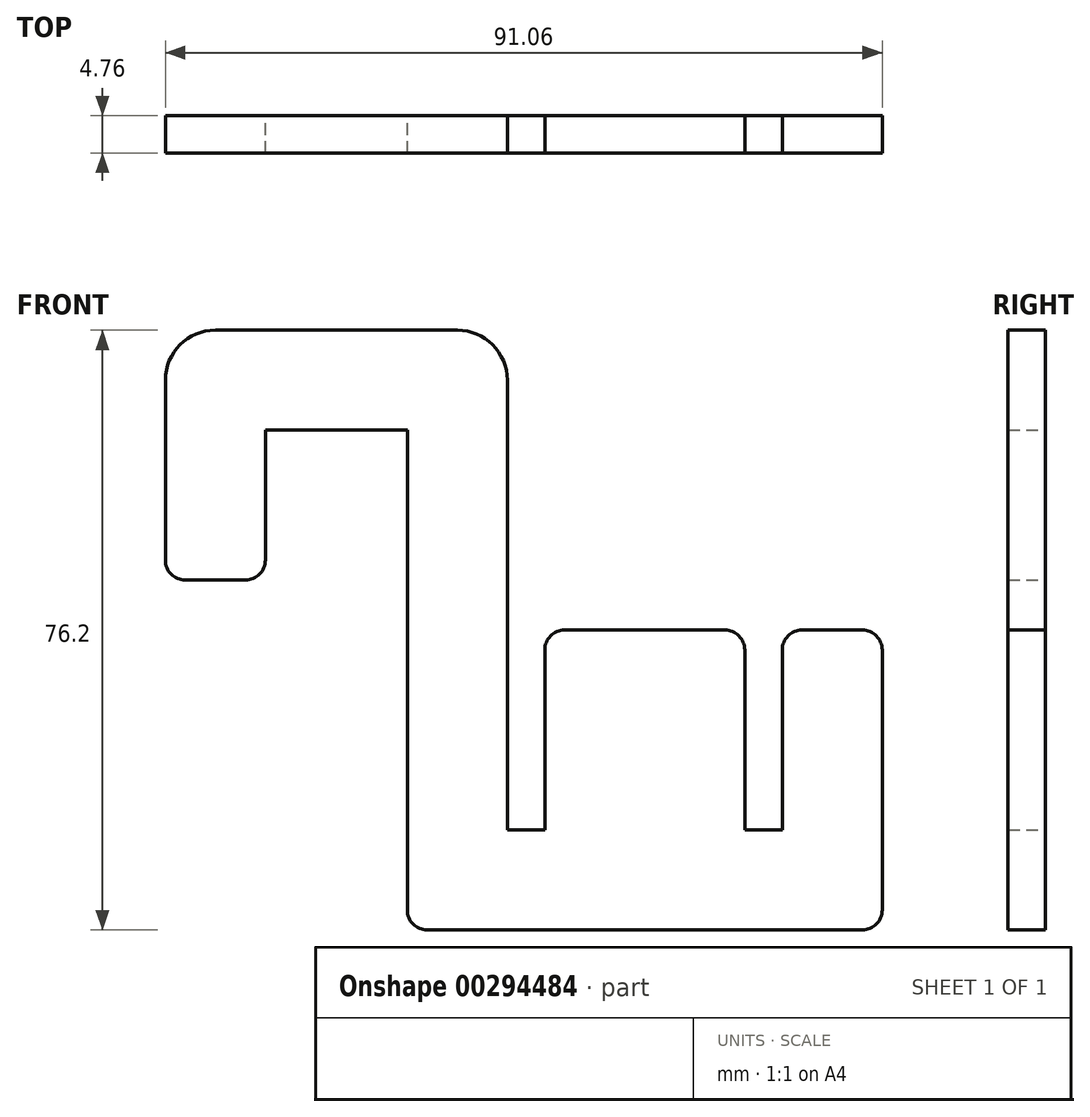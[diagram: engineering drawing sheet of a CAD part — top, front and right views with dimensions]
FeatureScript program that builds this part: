
annotation { "Feature Type Name" : "Feature", "Feature Type Description" : "" }
export const myFeature = defineFeature(function(context is Context, id is Id, definition is map)
    precondition{}
    {
        {
            var Q0;
            Q0=qCreatedBy(makeId("Front.planeOp"),FACE);
            var sketch = newSketch(context, id + "F0", { "sketchPlane" : qUnion([Q0])});
            skLineSegment(sketch, "E0.bottom", {"start": v(-2.54, 0) * mm, "end": v(-57.79, 0) * mm});
            skLineSegment(sketch, "E0.left", {"start": v(0, 2.54) * mm, "end": v(0, 35.56) * mm});
            skLineSegment(sketch, "E0.right", {"start": v(-60.33, 2.54) * mm, "end": v(-60.33, 63.5) * mm});
            skLineSegment(sketch, "E1.left", {"start": v(-47.63, 63.5) * mm, "end": v(-47.63, 12.7) * mm});
            skLineSegment(sketch, "E2.top", {"start": v(-12.7, 12.7) * mm, "end": v(-17.46, 12.7) * mm});
            skLineSegment(sketch, "E2.left", {"start": v(-12.7, 35.56) * mm, "end": v(-12.7, 12.7) * mm});
            skLineSegment(sketch, "E2.right", {"start": v(-17.46, 35.56) * mm, "end": v(-17.46, 12.7) * mm});
            skLineSegment(sketch, "E3.bottom", {"start": v(-60.33, 63.5) * mm, "end": v(-78.36, 63.5) * mm});
            skLineSegment(sketch, "E3.top", {"start": v(-53.98, 76.2) * mm, "end": v(-84.7, 76.2) * mm});
            skLineSegment(sketch, "E3.right", {"start": v(-91.06, 63.5) * mm, "end": v(-91.06, 69.85) * mm});
            skLineSegment(sketch, "E4.bottom", {"start": v(-84.7, 76.2) * mm, "end": v(-78.36, 76.2) * mm});
            skLineSegment(sketch, "E4.top", {"start": v(-88.52, 44.45) * mm, "end": v(-80.9, 44.45) * mm});
            skLineSegment(sketch, "E4.left", {"start": v(-91.06, 69.85) * mm, "end": v(-91.06, 46.99) * mm});
            skLineSegment(sketch, "E4.right", {"start": v(-78.36, 63.5) * mm, "end": v(-78.36, 46.99) * mm});
            skLineSegment(sketch, "E5.right", {"start": v(-47.63, 69.85) * mm, "end": v(-47.63, 63.5) * mm});
            skArc(sketch, "E6.filletArc", {"start": v(-47.63, 69.85) * mm, "mid": v(-49.48, 74.34) * mm, "end": v(-53.98, 76.2) * mm});
            skPoint(sketch, "E7.visualSharp", {"position": v(-91.06, 76.2) * mm});
            skArc(sketch, "E7.filletArc", {"start": v(-84.7, 76.2) * mm, "mid": v(-89.2, 74.34) * mm, "end": v(-91.06, 69.85) * mm});
            skLineSegment(sketch, "E8.top", {"start": v(-47.63, 12.7) * mm, "end": v(-42.86, 12.7) * mm});
            skLineSegment(sketch, "E8.left", {"start": v(-42.86, 35.56) * mm, "end": v(-42.86, 12.7) * mm});
            skLineSegment(sketch, "E9.trimOffspring", {"start": v(-10.16, 38.1) * mm, "end": v(-2.54, 38.1) * mm});
            skLineSegment(sketch, "E10", {"start": v(-40.32, 38.1) * mm, "end": v(-20, 38.1) * mm});
            skPoint(sketch, "E11.visualSharp", {"position": v(0, 38.1) * mm});
            skArc(sketch, "E11.filletArc", {"start": v(0, 35.56) * mm, "mid": v(-0.74, 37.36) * mm, "end": v(-2.54, 38.1) * mm});
            skPoint(sketch, "E12.visualSharp", {"position": v(-12.7, 38.1) * mm});
            skArc(sketch, "E12.filletArc", {"start": v(-10.16, 38.1) * mm, "mid": v(-11.96, 37.36) * mm, "end": v(-12.7, 35.56) * mm});
            skPoint(sketch, "E13.visualSharp", {"position": v(-17.46, 38.1) * mm});
            skArc(sketch, "E13.filletArc", {"start": v(-17.46, 35.56) * mm, "mid": v(-18.2, 37.36) * mm, "end": v(-20, 38.1) * mm});
            skPoint(sketch, "E14.visualSharp", {"position": v(-42.86, 38.1) * mm});
            skArc(sketch, "E14.filletArc", {"start": v(-40.32, 38.1) * mm, "mid": v(-42.12, 37.36) * mm, "end": v(-42.86, 35.56) * mm});
            skPoint(sketch, "E15.visualSharp", {"position": v(-60.33, 0) * mm});
            skArc(sketch, "E15.filletArc", {"start": v(-60.33, 2.54) * mm, "mid": v(-59.58, 0.74) * mm, "end": v(-57.79, 0) * mm});
            skPoint(sketch, "E16.visualSharp", {"position": v(0, 0) * mm});
            skArc(sketch, "E16.filletArc", {"start": v(-2.54, 0) * mm, "mid": v(-0.74, 0.74) * mm, "end": v(0, 2.54) * mm});
            skPoint(sketch, "E17.visualSharp", {"position": v(-91.06, 44.45) * mm});
            skArc(sketch, "E17.filletArc", {"start": v(-91.06, 46.99) * mm, "mid": v(-90.32, 45.2) * mm, "end": v(-88.52, 44.45) * mm});
            skPoint(sketch, "E18.visualSharp", {"position": v(-78.36, 44.45) * mm});
            skArc(sketch, "E18.filletArc", {"start": v(-80.9, 44.45) * mm, "mid": v(-79.1, 45.2) * mm, "end": v(-78.36, 46.99) * mm});
            skSolve(sketch);
        }
        {
            var Q0;
            Q0=makeQuery(id+"F0.imprint","IMPRINT",FACE,{"disambiguationData":[TD([[makeQuery(id+"F0.imprint","IMPRINT",EDGE,{"derivedFrom":sQuery(id+"F0.wireOp",EDGE,"E0.bottom")}),-1.0]])]});
            extrude(context, id + "F1", {"entities" : qUnion([Q0]), "depth" : 4.76 * mm});
        }
    });
